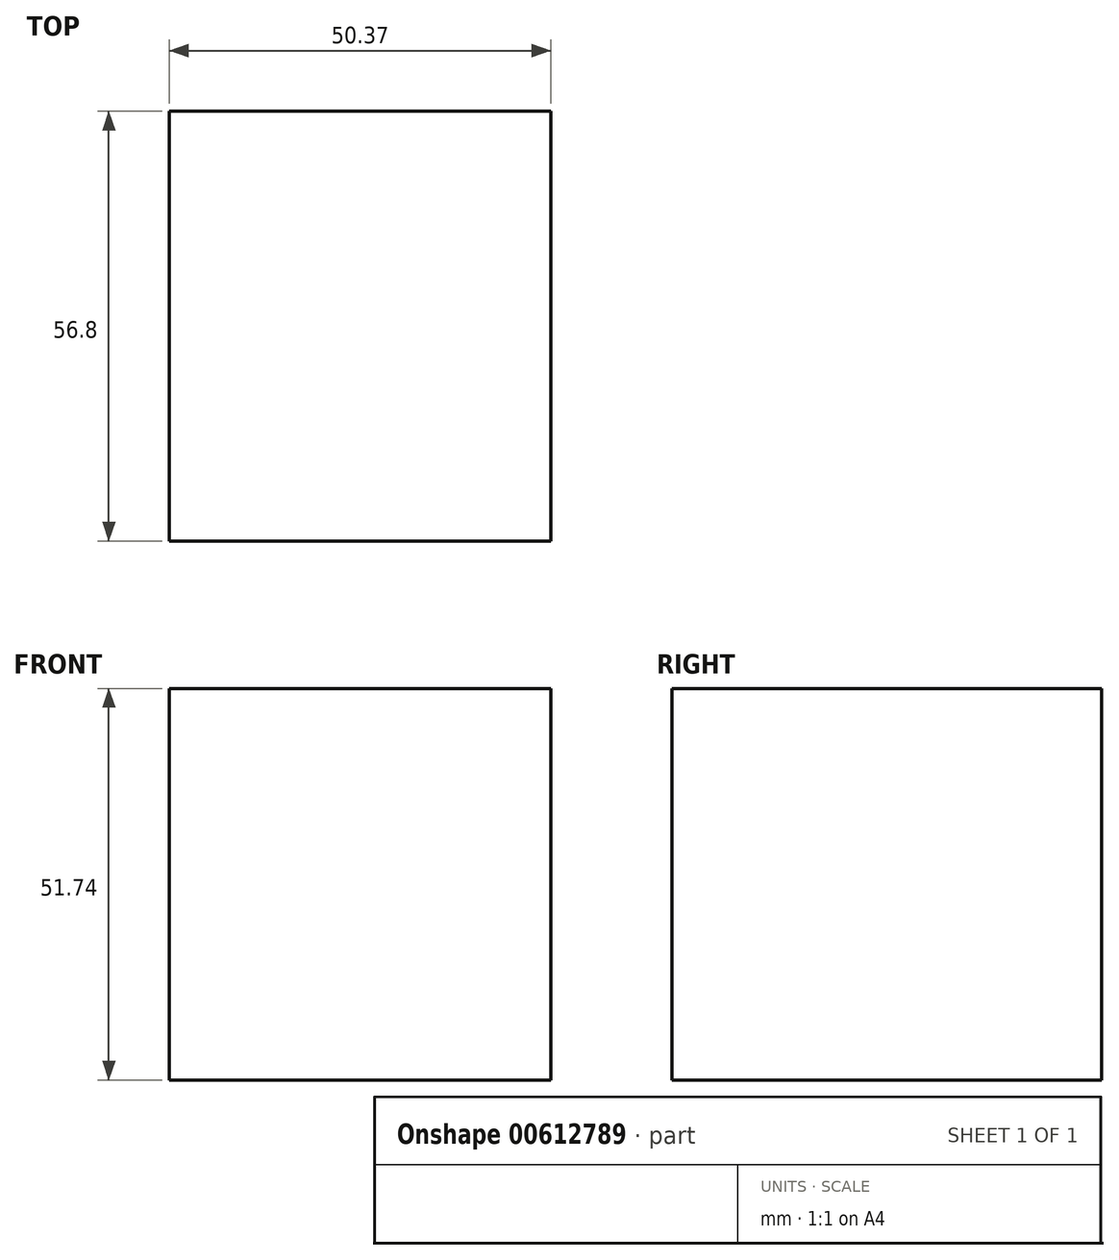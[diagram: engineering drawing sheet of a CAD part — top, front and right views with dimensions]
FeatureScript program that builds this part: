
annotation { "Feature Type Name" : "Feature", "Feature Type Description" : "" }
export const myFeature = defineFeature(function(context is Context, id is Id, definition is map)
    precondition{}
    {
        {
            var Q0;
            Q0=qCreatedBy(makeId("Top.planeOp"),FACE);
            var sketch = newSketch(context, id + "F0", { "sketchPlane" : qUnion([Q0])});
            skLineSegment(sketch, "E0.bottom", {"start": v(0, 0) * mm, "end": v(50.37, 0) * mm});
            skLineSegment(sketch, "E0.top", {"start": v(0, 56.8) * mm, "end": v(50.37, 56.8) * mm});
            skLineSegment(sketch, "E0.left", {"start": v(0, 0) * mm, "end": v(0, 56.8) * mm});
            skLineSegment(sketch, "E0.right", {"start": v(50.37, 0) * mm, "end": v(50.37, 56.8) * mm});
            skSolve(sketch);
        }
        {
            var Q0;
            Q0 = qSketchRegion(id + "F0", true);
            extrude(context, id + "F1", {"entities" : qUnion([Q0]), "depth" : 51.74 * mm, "offsetDistance" : 25 * mm});
        }
    });
